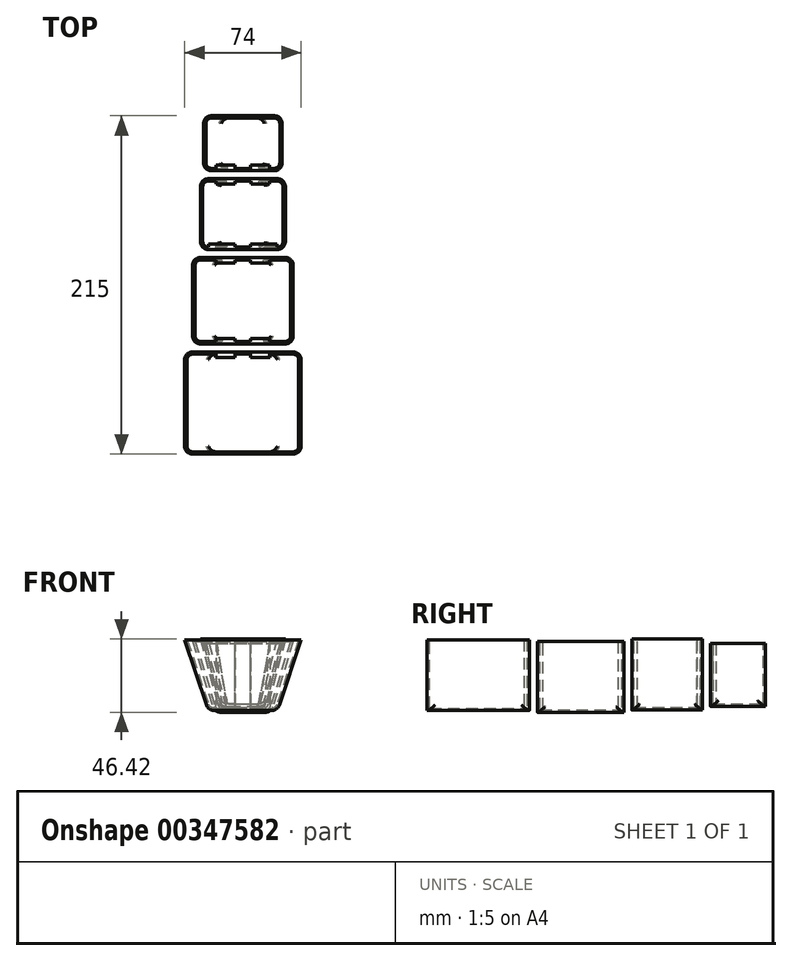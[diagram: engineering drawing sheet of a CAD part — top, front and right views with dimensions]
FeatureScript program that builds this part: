
annotation { "Feature Type Name" : "Feature", "Feature Type Description" : "" }
export const myFeature = defineFeature(function(context is Context, id is Id, definition is map)
    precondition{}
    {
        {
            var Q0;
            Q0=qCreatedBy(makeId("Front.planeOp"),FACE);
            var sketch = newSketch(context, id + "F0", { "sketchPlane" : qUnion([Q0])});
            skLineSegment(sketch, "E0", {"start": v(0, 23.9) * mm, "end": v(-37, 23.9) * mm});
            skLineSegment(sketch, "E1", {"start": v(-37, 23.9) * mm, "end": v(-22, -21.1) * mm});
            skLineSegment(sketch, "E2", {"start": v(-22, -21.1) * mm, "end": v(0, -21.1) * mm});
            skLineSegment(sketch, "E3.MirrorCS", {"start": v(0, 23.9) * mm, "end": v(37, 23.9) * mm});
            skLineSegment(sketch, "E4.MirrorCS", {"start": v(37, 23.9) * mm, "end": v(22, -21.1) * mm});
            skLineSegment(sketch, "E5.MirrorCS", {"start": v(22, -21.1) * mm, "end": v(0, -21.1) * mm});
            skSolve(sketch);
        }
        {
            var Q0;
            Q0=makeQuery(id+"F0.imprint","IMPRINT",FACE,{"disambiguationData":[TD([[makeQuery(id+"F0.imprint","IMPRINT",EDGE,{"derivedFrom":sQuery(id+"F0.wireOp",EDGE,"E0")}),1.0]])]});
            extrude(context, id + "F1", {"entities" : qUnion([Q0]), "depth" : 65 * mm});
        }
        {
            var Q0;
            Q0=makeQuery(id+"F1.opExtrude","SWEPT_EDGE",EDGE,{"disambiguationData":[OSD([sQuery(id+"F0.wireOp",EDGE,"E1"),sQuery(id+"F0.wireOp",EDGE,"E2")])]});
            var Q1;
            Q1=makeQuery(id+"F1.opExtrude","SWEPT_EDGE",EDGE,{"disambiguationData":[OSD([sQuery(id+"F0.wireOp",EDGE,"E4.MirrorCS"),sQuery(id+"F0.wireOp",EDGE,"E5.MirrorCS")])]});
            var Q2;
            Q2=makeQuery(id+"F1.opExtrude","CAP_EDGE",EDGE,{"disambiguationData":[OSD([sQuery(id+"F0.wireOp",EDGE,"E1")])],"isStart":false});
            var Q3;
            Q3=makeQuery(id+"F1.opExtrude","CAP_EDGE",EDGE,{"disambiguationData":[OSD([sQuery(id+"F0.wireOp",EDGE,"E4.MirrorCS")])],"isStart":false});
            var Q4;
            Q4=makeQuery(id+"F1.opExtrude","CAP_EDGE",EDGE,{"disambiguationData":[OSD([sQuery(id+"F0.wireOp",EDGE,"E4.MirrorCS")])],"isStart":true});
            var Q5;
            Q5=makeQuery(id+"F1.opExtrude","CAP_EDGE",EDGE,{"disambiguationData":[OSD([sQuery(id+"F0.wireOp",EDGE,"E1")])],"isStart":true});
            fillet(context, id + "F2", {"entities" : qUnion([Q0, Q1, Q2, Q3, Q4, Q5]), "radius" : 5 * mm, "tangentPropagation" : true, "allowEdgeOverflow" : false});
        }
        {
            var Q0;
            Q0=qCreatedBy(makeId("Front.planeOp"),FACE);
            cPlane(context, id + "F3", {"entities" : qUnion([Q0]), "cplaneType" : CPlaneType.OFFSET, "offset" : 60 * mm, "oppositeDirection" : true, "width" : 150 * mm, "height" : 150 * mm});
        }
        {
            var Q0;
            Q0=qCreatedBy(id+"F3.planeOp",FACE);
            var sketch = newSketch(context, id + "F4", { "sketchPlane" : qUnion([Q0])});
            skLineSegment(sketch, "E6", {"start": v(0, 22.82) * mm, "end": v(32, 22.82) * mm});
            skLineSegment(sketch, "E7", {"start": v(32, 22.82) * mm, "end": v(18, -22.18) * mm});
            skLineSegment(sketch, "E8", {"start": v(18, -22.18) * mm, "end": v(0, -22.18) * mm});
            skLineSegment(sketch, "E9.MirrorCS", {"start": v(0, 22.82) * mm, "end": v(-32, 22.82) * mm});
            skLineSegment(sketch, "E10.MirrorCS", {"start": v(-32, 22.82) * mm, "end": v(-18, -22.18) * mm});
            skLineSegment(sketch, "E11.MirrorCS", {"start": v(-18, -22.18) * mm, "end": v(0, -22.18) * mm});
            skSolve(sketch);
        }
        {
            var Q0;
            Q0=makeQuery(id+"F4.imprint","IMPRINT",FACE,{"disambiguationData":[TD([[makeQuery(id+"F4.imprint","IMPRINT",EDGE,{"derivedFrom":sQuery(id+"F4.wireOp",EDGE,"E6")}),-1.0]])]});
            extrude(context, id + "F5", {"entities" : qUnion([Q0]), "depth" : 55 * mm});
        }
        {
            var Q0;
            Q0=makeQuery(id+"F5.opExtrude","CAP_EDGE",EDGE,{"disambiguationData":[OSD([sQuery(id+"F4.wireOp",EDGE,"E7")])],"isStart":true});
            var Q1;
            Q1=makeQuery(id+"F5.opExtrude","CAP_EDGE",EDGE,{"disambiguationData":[OSD([sQuery(id+"F4.wireOp",EDGE,"E10.MirrorCS")])],"isStart":true});
            var Q2;
            Q2=makeQuery(id+"F5.opExtrude","SWEPT_EDGE",EDGE,{"disambiguationData":[OSD([sQuery(id+"F4.wireOp",EDGE,"E7"),sQuery(id+"F4.wireOp",EDGE,"E8")])]});
            var Q3;
            Q3=makeQuery(id+"F5.opExtrude","SWEPT_EDGE",EDGE,{"disambiguationData":[OSD([sQuery(id+"F4.wireOp",EDGE,"E10.MirrorCS"),sQuery(id+"F4.wireOp",EDGE,"E11.MirrorCS")])]});
            var Q4;
            Q4=makeQuery(id+"F5.opExtrude","CAP_EDGE",EDGE,{"disambiguationData":[OSD([sQuery(id+"F4.wireOp",EDGE,"E10.MirrorCS")])],"isStart":false});
            var Q5;
            Q5=makeQuery(id+"F5.opExtrude","CAP_EDGE",EDGE,{"disambiguationData":[OSD([sQuery(id+"F4.wireOp",EDGE,"E7")])],"isStart":false});
            fillet(context, id + "F6", {"entities" : qUnion([Q0, Q1, Q2, Q3, Q4, Q5]), "radius" : 5 * mm, "tangentPropagation" : true, "allowEdgeOverflow" : false});
        }
        {
            var Q0;
            Q0=qCreatedBy(id+"F3.planeOp",FACE);
            cPlane(context, id + "F7", {"entities" : qUnion([Q0]), "cplaneType" : CPlaneType.OFFSET, "offset" : 50 * mm, "oppositeDirection" : true, "width" : 150 * mm, "height" : 150 * mm});
        }
        {
            var Q0;
            Q0=qCreatedBy(id+"F7.planeOp",FACE);
            var sketch = newSketch(context, id + "F8", { "sketchPlane" : qUnion([Q0])});
            skLineSegment(sketch, "E12", {"start": v(0, 24.24) * mm, "end": v(27, 24.24) * mm});
            skLineSegment(sketch, "E13", {"start": v(27, 24.24) * mm, "end": v(15, -20.76) * mm});
            skLineSegment(sketch, "E14", {"start": v(15, -20.76) * mm, "end": v(0, -20.76) * mm});
            skLineSegment(sketch, "E15.MirrorCS", {"start": v(0, 24.24) * mm, "end": v(-27, 24.24) * mm});
            skLineSegment(sketch, "E16.MirrorCS", {"start": v(-27, 24.24) * mm, "end": v(-15, -20.76) * mm});
            skLineSegment(sketch, "E17.MirrorCS", {"start": v(-15, -20.76) * mm, "end": v(0, -20.76) * mm});
            skSolve(sketch);
        }
        {
            var Q0;
            Q0=makeQuery(id+"F8.imprint","IMPRINT",FACE,{"disambiguationData":[TD([[makeQuery(id+"F8.imprint","IMPRINT",EDGE,{"derivedFrom":sQuery(id+"F8.wireOp",EDGE,"E12")}),-1.0]])]});
            extrude(context, id + "F9", {"entities" : qUnion([Q0]), "depth" : 45 * mm});
        }
        {
            var Q0;
            Q0=makeQuery(id+"F9.opExtrude","CAP_EDGE",EDGE,{"disambiguationData":[OSD([sQuery(id+"F8.wireOp",EDGE,"E13")])],"isStart":true});
            var Q1;
            Q1=makeQuery(id+"F9.opExtrude","CAP_EDGE",EDGE,{"disambiguationData":[OSD([sQuery(id+"F8.wireOp",EDGE,"E16.MirrorCS")])],"isStart":true});
            var Q2;
            Q2=makeQuery(id+"F9.opExtrude","SWEPT_EDGE",EDGE,{"disambiguationData":[OSD([sQuery(id+"F8.wireOp",EDGE,"E13"),sQuery(id+"F8.wireOp",EDGE,"E14")])]});
            var Q3;
            Q3=makeQuery(id+"F9.opExtrude","SWEPT_EDGE",EDGE,{"disambiguationData":[OSD([sQuery(id+"F8.wireOp",EDGE,"E16.MirrorCS"),sQuery(id+"F8.wireOp",EDGE,"E17.MirrorCS")])]});
            var Q4;
            Q4=makeQuery(id+"F9.opExtrude","CAP_EDGE",EDGE,{"disambiguationData":[OSD([sQuery(id+"F8.wireOp",EDGE,"E13")])],"isStart":false});
            var Q5;
            Q5=makeQuery(id+"F9.opExtrude","CAP_EDGE",EDGE,{"disambiguationData":[OSD([sQuery(id+"F8.wireOp",EDGE,"E16.MirrorCS")])],"isStart":false});
            fillet(context, id + "F10", {"entities" : qUnion([Q0, Q1, Q2, Q3, Q4, Q5]), "radius" : 5 * mm, "tangentPropagation" : true, "allowEdgeOverflow" : false});
        }
        {
            var Q0;
            Q0=qCreatedBy(id+"F7.planeOp",FACE);
            cPlane(context, id + "F11", {"entities" : qUnion([Q0]), "cplaneType" : CPlaneType.OFFSET, "offset" : 40 * mm, "oppositeDirection" : true, "width" : 150 * mm, "height" : 150 * mm});
        }
        {
            var Q0;
            Q0=qCreatedBy(id+"F11.planeOp",FACE);
            var sketch = newSketch(context, id + "F12", { "sketchPlane" : qUnion([Q0])});
            skLineSegment(sketch, "E18", {"start": v(0, 21.5) * mm, "end": v(25, 21.5) * mm});
            skLineSegment(sketch, "E19", {"start": v(25, 21.5) * mm, "end": v(14, -18.5) * mm});
            skLineSegment(sketch, "E20", {"start": v(14, -18.5) * mm, "end": v(0, -18.5) * mm});
            skLineSegment(sketch, "E21.MirrorCS", {"start": v(0, 21.5) * mm, "end": v(-25, 21.5) * mm});
            skLineSegment(sketch, "E22.MirrorCS", {"start": v(-25, 21.5) * mm, "end": v(-14, -18.5) * mm});
            skLineSegment(sketch, "E23.MirrorCS", {"start": v(-14, -18.5) * mm, "end": v(0, -18.5) * mm});
            skSolve(sketch);
        }
        {
            var Q0;
            Q0=makeQuery(id+"F12.imprint","IMPRINT",FACE,{"disambiguationData":[TD([[makeQuery(id+"F12.imprint","IMPRINT",EDGE,{"derivedFrom":sQuery(id+"F12.wireOp",EDGE,"E18")}),-1.0]])]});
            extrude(context, id + "F13", {"entities" : qUnion([Q0]), "depth" : 35 * mm});
        }
        {
            var Q0;
            Q0=makeQuery(id+"F13.opExtrude","CAP_EDGE",EDGE,{"disambiguationData":[OSD([sQuery(id+"F12.wireOp",EDGE,"E19")])],"isStart":true});
            var Q1;
            Q1=makeQuery(id+"F13.opExtrude","CAP_EDGE",EDGE,{"disambiguationData":[OSD([sQuery(id+"F12.wireOp",EDGE,"E22.MirrorCS")])],"isStart":true});
            var Q2;
            Q2=makeQuery(id+"F13.opExtrude","SWEPT_EDGE",EDGE,{"disambiguationData":[OSD([sQuery(id+"F12.wireOp",EDGE,"E19"),sQuery(id+"F12.wireOp",EDGE,"E20")])]});
            var Q3;
            Q3=makeQuery(id+"F13.opExtrude","SWEPT_EDGE",EDGE,{"disambiguationData":[OSD([sQuery(id+"F12.wireOp",EDGE,"E22.MirrorCS"),sQuery(id+"F12.wireOp",EDGE,"E23.MirrorCS")])]});
            var Q4;
            Q4=makeQuery(id+"F13.opExtrude","CAP_EDGE",EDGE,{"disambiguationData":[OSD([sQuery(id+"F12.wireOp",EDGE,"E19")])],"isStart":false});
            var Q5;
            Q5=makeQuery(id+"F13.opExtrude","CAP_EDGE",EDGE,{"disambiguationData":[OSD([sQuery(id+"F12.wireOp",EDGE,"E22.MirrorCS")])],"isStart":false});
            fillet(context, id + "F14", {"entities" : qUnion([Q0, Q1, Q2, Q3, Q4, Q5]), "radius" : 5 * mm, "tangentPropagation" : true, "allowEdgeOverflow" : false});
        }
        {
            var Q0;
            Q0=makeQuery(id+"F5.opExtrude","SWEPT_FACE",FACE,{"disambiguationData":[OSD([sQuery(id+"F4.wireOp",EDGE,"E6"),sQuery(id+"F4.wireOp",EDGE,"E9.MirrorCS")])]});
            shell(context, id + "F15", {"entities" : qUnion([Q0]), "thickness" : 1.6 * mm});
        }
        {
            var Q0;
            Q0=makeQuery(id+"F13.opExtrude","SWEPT_FACE",FACE,{"disambiguationData":[OSD([sQuery(id+"F12.wireOp",EDGE,"E18"),sQuery(id+"F12.wireOp",EDGE,"E21.MirrorCS")])]});
            shell(context, id + "F16", {"entities" : qUnion([Q0]), "thickness" : 1.5 * mm});
        }
        {
            var Q0;
            Q0=makeQuery(id+"F1.opExtrude","SWEPT_FACE",FACE,{"disambiguationData":[OSD([sQuery(id+"F0.wireOp",EDGE,"E0"),sQuery(id+"F0.wireOp",EDGE,"E3.MirrorCS")])]});
            shell(context, id + "F17", {"entities" : qUnion([Q0]), "thickness" : 1.5 * mm});
        }
        {
            var Q0;
            Q0=makeQuery(id+"F9.opExtrude","SWEPT_FACE",FACE,{"disambiguationData":[OSD([sQuery(id+"F8.wireOp",EDGE,"E12"),sQuery(id+"F8.wireOp",EDGE,"E15.MirrorCS")])]});
            shell(context, id + "F18", {"entities" : qUnion([Q0]), "thickness" : 1.5 * mm});
        }
        {
            var Q0;
            {var subQ0=sQuery(id+"F8.wireOp",EDGE,"E17.MirrorCS");var subQ1=sQuery(id+"F8.wireOp",EDGE,"E16.MirrorCS");var subQ2=sQuery(id+"F8.wireOp",EDGE,"E15.MirrorCS");var subQ3=sQuery(id+"F8.wireOp",EDGE,"E14");var subQ4=sQuery(id+"F8.wireOp",EDGE,"E13");var subQ5=sQuery(id+"F8.wireOp",EDGE,"E12");Q0=makeQuery(id+"F18.opShell","OFFSET_FACE",FACE,{"disambiguationData":[OSD([subQ5,subQ4,subQ3,subQ2,subQ1,subQ0]),TDD([makeQuery(id+"F9.opExtrude","CAP_FACE",FACE,{"disambiguationData":[OSD([subQ5,subQ4,subQ3,subQ2,subQ1,subQ0])],"isStart":true})])]});}
            var sketch = newSketch(context, id + "F19", { "sketchPlane" : qUnion([Q0])});
            skLineSegment(sketch, "E24", {"start": v(-5, -19.26) * mm, "end": v(-5, 24.24) * mm});
            skLineSegment(sketch, "E25", {"start": v(-5, 24.24) * mm, "end": v(-17, 24.24) * mm});
            skLineSegment(sketch, "E26", {"start": v(-17, 24.24) * mm, "end": v(-10.23, -19.26) * mm});
            skLineSegment(sketch, "E27", {"start": v(-10.23, -19.26) * mm, "end": v(-5, -19.26) * mm});
            skLineSegment(sketch, "E28", {"start": v(0.03, -19.26) * mm, "end": v(0.03, 24.24) * mm, "construction": true});
            skLineSegment(sketch, "E29.MirrorCS", {"start": v(5.05, -19.26) * mm, "end": v(5.05, 24.24) * mm});
            skLineSegment(sketch, "E30.MirrorCS", {"start": v(5.05, 24.24) * mm, "end": v(17.05, 24.24) * mm});
            skLineSegment(sketch, "E31.MirrorCS", {"start": v(17.05, 24.24) * mm, "end": v(10.28, -19.26) * mm});
            skLineSegment(sketch, "E32.MirrorCS", {"start": v(10.28, -19.26) * mm, "end": v(5.05, -19.26) * mm});
            skSolve(sketch);
        }
        {
            var Q0;
            Q0=makeQuery(id+"F19.imprint","IMPRINT",FACE,{"disambiguationData":[TD([[makeQuery(id+"F19.imprint","IMPRINT",EDGE,{"derivedFrom":sQuery(id+"F19.wireOp",EDGE,"0ba9f9f1-b0b3-4cc9-8b6a-4698d6627ffc0.MirrorCS")}),-1.0]])]});
            var Q1;
            Q1=makeQuery(id+"F19.imprint","IMPRINT",FACE,{"disambiguationData":[TD([[makeQuery(id+"F19.imprint","IMPRINT",EDGE,{"derivedFrom":sQuery(id+"F19.wireOp",EDGE,"E24")}),1.0]])]});
            var Q2;
            {var subQ12=sQuery(id+"F19.wireOp",EDGE,"E29.MirrorCS");Q2=makeQuery(id+"F19.imprint","IMPRINT",FACE,{"disambiguationData":[TD([[makeQuery(id+"F19.imprint","IMPRINT",EDGE,{"derivedFrom":subQ12}),-1.0]])]});}
            extrude(context, id + "F20", {"entities" : qUnion([Q0, Q1, Q2]), "operationType" : NewBodyOperationType.ADD, "depth" : 2 * mm});
        }
        {
            var Q0;
            {var subQ0=sQuery(id+"F8.wireOp",EDGE,"E17.MirrorCS");var subQ1=sQuery(id+"F8.wireOp",EDGE,"E16.MirrorCS");var subQ2=sQuery(id+"F8.wireOp",EDGE,"E15.MirrorCS");var subQ3=sQuery(id+"F8.wireOp",EDGE,"E14");var subQ4=sQuery(id+"F8.wireOp",EDGE,"E13");var subQ5=sQuery(id+"F8.wireOp",EDGE,"E12");Q0=makeQuery(id+"F18.opShell","OFFSET_FACE",FACE,{"disambiguationData":[OSD([subQ5,subQ4,subQ3,subQ2,subQ1,subQ0]),TDD([makeQuery(id+"F9.opExtrude","CAP_FACE",FACE,{"disambiguationData":[OSD([subQ5,subQ4,subQ3,subQ2,subQ1,subQ0])],"isStart":false})])]});}
            var sketch = newSketch(context, id + "F21", { "sketchPlane" : qUnion([Q0])});
            skLineSegment(sketch, "E33", {"start": v(0, -19.26) * mm, "end": v(0, 24.24) * mm, "construction": true});
            skPoint(sketch, "E34.0", {"position": v(-10.23, -19.26) * mm});
            skPoint(sketch, "E35.0", {"position": v(10.23, -19.26) * mm});
            skPoint(sketch, "E36.0", {"position": v(21.83, 24.24) * mm});
            skPoint(sketch, "E37.0", {"position": v(-21.83, 24.24) * mm});
            skLineSegment(sketch, "E38.0", {"start": v(10.23, -19.26) * mm, "end": v(-10.23, -19.26) * mm});
            skLineSegment(sketch, "E39", {"start": v(-5, -19.26) * mm, "end": v(-5, 24.24) * mm});
            skLineSegment(sketch, "E40", {"start": v(-5, -19.26) * mm, "end": v(-10.23, -19.26) * mm});
            skLineSegment(sketch, "E41", {"start": v(-21.83, 24.24) * mm, "end": v(-5, 24.24) * mm});
            skLineSegment(sketch, "E42.MirrorCS", {"start": v(5, -19.26) * mm, "end": v(5, 24.24) * mm});
            skLineSegment(sketch, "E43.MirrorCS", {"start": v(5, -19.26) * mm, "end": v(10.23, -19.26) * mm});
            skLineSegment(sketch, "E44.MirrorCS", {"start": v(21.83, 24.24) * mm, "end": v(5, 24.24) * mm});
            skLineSegment(sketch, "E45", {"start": v(-10.23, -19.26) * mm, "end": v(-21.83, 24.24) * mm});
            skLineSegment(sketch, "E46.MirrorCS", {"start": v(10.23, -19.26) * mm, "end": v(21.83, 24.24) * mm});
            skSolve(sketch);
        }
        {
            var Q0;
            Q0=makeQuery(id+"F21.imprint","IMPRINT",FACE,{"disambiguationData":[TD([[makeQuery(id+"F21.imprint","IMPRINT",EDGE,{"derivedFrom":sQuery(id+"F21.wireOp",EDGE,"E39")}),1.0]])]});
            var Q1;
            Q1=makeQuery(id+"F21.imprint","IMPRINT",FACE,{"disambiguationData":[TD([[makeQuery(id+"F21.imprint","IMPRINT",EDGE,{"derivedFrom":sQuery(id+"F21.wireOp",EDGE,"E42.MirrorCS")}),-1.0]])]});
            extrude(context, id + "F22", {"entities" : qUnion([Q0, Q1]), "operationType" : NewBodyOperationType.ADD, "depth" : 2 * mm});
        }
        {
            var Q0;
            {var subQ0=sQuery(id+"F12.wireOp",EDGE,"E23.MirrorCS");var subQ1=sQuery(id+"F12.wireOp",EDGE,"E22.MirrorCS");var subQ2=sQuery(id+"F12.wireOp",EDGE,"E21.MirrorCS");var subQ3=sQuery(id+"F12.wireOp",EDGE,"E20");var subQ4=sQuery(id+"F12.wireOp",EDGE,"E19");var subQ5=sQuery(id+"F12.wireOp",EDGE,"E18");Q0=makeQuery(id+"F16.opShell","OFFSET_FACE",FACE,{"disambiguationData":[OSD([subQ5,subQ4,subQ3,subQ2,subQ1,subQ0]),TDD([makeQuery(id+"F13.opExtrude","CAP_FACE",FACE,{"disambiguationData":[OSD([subQ5,subQ4,subQ3,subQ2,subQ1,subQ0])],"isStart":false})])]});}
            var sketch = newSketch(context, id + "F23", { "sketchPlane" : qUnion([Q0])});
            skLineSegment(sketch, "E47", {"start": v(0, -17) * mm, "end": v(0, 21.5) * mm, "construction": true});
            skLineSegment(sketch, "E48", {"start": v(-5, -17) * mm, "end": v(-5, 21.5) * mm});
            skLineSegment(sketch, "E49", {"start": v(-5, -17) * mm, "end": v(-10, -17) * mm});
            skLineSegment(sketch, "E50", {"start": v(-17, 21.5) * mm, "end": v(-5, 21.5) * mm});
            skLineSegment(sketch, "E51.MirrorCS", {"start": v(5, -17) * mm, "end": v(5, 21.5) * mm});
            skLineSegment(sketch, "E52.MirrorCS", {"start": v(5, -17) * mm, "end": v(10, -17) * mm});
            skLineSegment(sketch, "E53.MirrorCS", {"start": v(17, 21.5) * mm, "end": v(5, 21.5) * mm});
            skLineSegment(sketch, "E54", {"start": v(-17, 21.5) * mm, "end": v(-10, -17) * mm});
            skLineSegment(sketch, "E55", {"start": v(17, 21.5) * mm, "end": v(10, -17) * mm});
            skSolve(sketch);
        }
        {
            var Q0;
            Q0 = qSketchRegion(id + "F23", true);
            var Q1;
            Q1=makeQuery(id+"F23.imprint","IMPRINT",FACE,{"disambiguationData":[TD([[makeQuery(id+"F23.imprint","IMPRINT",EDGE,{"derivedFrom":sQuery(id+"F23.wireOp",EDGE,"E51.MirrorCS")}),-1.0]])]});
            extrude(context, id + "F24", {"entities" : qUnion([Q0, Q1]), "operationType" : NewBodyOperationType.ADD, "depth" : 2 * mm});
        }
        {
            var Q0;
            {var subQ0=sQuery(id+"F4.wireOp",EDGE,"E11.MirrorCS");var subQ1=sQuery(id+"F4.wireOp",EDGE,"E10.MirrorCS");var subQ2=sQuery(id+"F4.wireOp",EDGE,"E9.MirrorCS");var subQ3=sQuery(id+"F4.wireOp",EDGE,"E8");var subQ4=sQuery(id+"F4.wireOp",EDGE,"E7");var subQ5=sQuery(id+"F4.wireOp",EDGE,"E6");Q0=makeQuery(id+"F15.opShell","OFFSET_FACE",FACE,{"disambiguationData":[OSD([subQ5,subQ4,subQ3,subQ2,subQ1,subQ0]),TDD([makeQuery(id+"F5.opExtrude","CAP_FACE",FACE,{"disambiguationData":[OSD([subQ5,subQ4,subQ3,subQ2,subQ1,subQ0])],"isStart":true})])]});}
            var sketch = newSketch(context, id + "F25", { "sketchPlane" : qUnion([Q0])});
            skLineSegment(sketch, "E56", {"start": v(0, 22.82) * mm, "end": v(0, -20.58) * mm, "construction": true});
            skLineSegment(sketch, "E57", {"start": v(-5, 22.82) * mm, "end": v(-5, -20.58) * mm});
            skLineSegment(sketch, "E58", {"start": v(-5, 22.82) * mm, "end": v(-17, 22.82) * mm});
            skLineSegment(sketch, "E59", {"start": v(-17, 22.82) * mm, "end": v(-13.26, -20.58) * mm});
            skLineSegment(sketch, "E60", {"start": v(-13.26, -20.58) * mm, "end": v(-5, -20.58) * mm});
            skLineSegment(sketch, "E61.MirrorCS", {"start": v(5, 22.82) * mm, "end": v(5, -20.58) * mm});
            skLineSegment(sketch, "E62.MirrorCS", {"start": v(5, 22.82) * mm, "end": v(17, 22.82) * mm});
            skLineSegment(sketch, "E63.MirrorCS", {"start": v(17, 22.82) * mm, "end": v(13.26, -20.58) * mm});
            skLineSegment(sketch, "E64.MirrorCS", {"start": v(13.26, -20.58) * mm, "end": v(5, -20.58) * mm});
            skSolve(sketch);
        }
        {
            var Q0;
            Q0 = qSketchRegion(id + "F25", true);
            extrude(context, id + "F26", {"entities" : qUnion([Q0]), "operationType" : NewBodyOperationType.ADD, "depth" : 2 * mm});
        }
        {
            var Q0;
            {var subQ0=sQuery(id+"F4.wireOp",EDGE,"E11.MirrorCS");var subQ1=sQuery(id+"F4.wireOp",EDGE,"E10.MirrorCS");var subQ2=sQuery(id+"F4.wireOp",EDGE,"E9.MirrorCS");var subQ3=sQuery(id+"F4.wireOp",EDGE,"E8");var subQ4=sQuery(id+"F4.wireOp",EDGE,"E7");var subQ5=sQuery(id+"F4.wireOp",EDGE,"E6");Q0=makeQuery(id+"F15.opShell","OFFSET_FACE",FACE,{"disambiguationData":[OSD([subQ5,subQ4,subQ3,subQ2,subQ1,subQ0]),TDD([makeQuery(id+"F5.opExtrude","CAP_FACE",FACE,{"disambiguationData":[OSD([subQ5,subQ4,subQ3,subQ2,subQ1,subQ0])],"isStart":false})])]});}
            var sketch = newSketch(context, id + "F27", { "sketchPlane" : qUnion([Q0])});
            skLineSegment(sketch, "E65", {"start": v(0, -20.58) * mm, "end": v(0, 22.82) * mm, "construction": true});
            skLineSegment(sketch, "E66", {"start": v(-5, -20.58) * mm, "end": v(-5, 22.82) * mm});
            skLineSegment(sketch, "E67", {"start": v(-5, -20.58) * mm, "end": v(-13.26, -20.58) * mm});
            skLineSegment(sketch, "E68", {"start": v(-13.26, -20.58) * mm, "end": v(-17, 22.82) * mm});
            skLineSegment(sketch, "E69", {"start": v(-17, 22.82) * mm, "end": v(-5, 22.82) * mm});
            skLineSegment(sketch, "E70.MirrorCS", {"start": v(5, -20.58) * mm, "end": v(5, 22.82) * mm});
            skLineSegment(sketch, "E71.MirrorCS", {"start": v(5, -20.58) * mm, "end": v(13.26, -20.58) * mm});
            skLineSegment(sketch, "E72.MirrorCS", {"start": v(13.26, -20.58) * mm, "end": v(17, 22.82) * mm});
            skLineSegment(sketch, "E73.MirrorCS", {"start": v(17, 22.82) * mm, "end": v(5, 22.82) * mm});
            skSolve(sketch);
        }
        {
            var Q0;
            Q0=makeQuery(id+"F27.imprint","IMPRINT",FACE,{"disambiguationData":[TD([[makeQuery(id+"F27.imprint","IMPRINT",EDGE,{"derivedFrom":sQuery(id+"F27.wireOp",EDGE,"E70.MirrorCS")}),-1.0]])]});
            var Q1;
            Q1=makeQuery(id+"F27.imprint","IMPRINT",FACE,{"disambiguationData":[TD([[makeQuery(id+"F27.imprint","IMPRINT",EDGE,{"derivedFrom":sQuery(id+"F27.wireOp",EDGE,"E66")}),1.0]])]});
            extrude(context, id + "F28", {"entities" : qUnion([Q0, Q1]), "operationType" : NewBodyOperationType.ADD, "depth" : 2 * mm});
        }
        {
            var Q0;
            {var subQ0=sQuery(id+"F0.wireOp",EDGE,"E5.MirrorCS");var subQ1=sQuery(id+"F0.wireOp",EDGE,"E4.MirrorCS");var subQ2=sQuery(id+"F0.wireOp",EDGE,"E3.MirrorCS");var subQ3=sQuery(id+"F0.wireOp",EDGE,"E2");var subQ4=sQuery(id+"F0.wireOp",EDGE,"E1");var subQ5=sQuery(id+"F0.wireOp",EDGE,"E0");Q0=makeQuery(id+"F17.opShell","OFFSET_FACE",FACE,{"disambiguationData":[OSD([subQ5,subQ4,subQ3,subQ2,subQ1,subQ0]),TDD([makeQuery(id+"F1.opExtrude","CAP_FACE",FACE,{"disambiguationData":[OSD([subQ5,subQ4,subQ3,subQ2,subQ1,subQ0])],"isStart":true})])]});}
            var sketch = newSketch(context, id + "F29", { "sketchPlane" : qUnion([Q0])});
            skLineSegment(sketch, "E74", {"start": v(0, -19.6) * mm, "end": v(0, 23.9) * mm, "construction": true});
            skLineSegment(sketch, "E75", {"start": v(-5, 23.9) * mm, "end": v(-5, -19.6) * mm});
            skLineSegment(sketch, "E76", {"start": v(-5, 23.9) * mm, "end": v(-31.73, 23.9) * mm});
            skLineSegment(sketch, "E77", {"start": v(-17, 23.9) * mm, "end": v(-17.23, -19.6) * mm});
            skLineSegment(sketch, "E78", {"start": v(-17.23, -19.6) * mm, "end": v(-5, -19.6) * mm});
            skLineSegment(sketch, "E79.MirrorCS", {"start": v(5, 23.9) * mm, "end": v(5, -19.6) * mm});
            skLineSegment(sketch, "E80.MirrorCS", {"start": v(5, 23.9) * mm, "end": v(31.73, 23.9) * mm});
            skLineSegment(sketch, "E81.MirrorCS", {"start": v(17, 23.9) * mm, "end": v(17.23, -19.6) * mm});
            skLineSegment(sketch, "E82.MirrorCS", {"start": v(17.23, -19.6) * mm, "end": v(5, -19.6) * mm});
            skSolve(sketch);
        }
        {
            var Q0;
            Q0 = qSketchRegion(id + "F29", true);
            extrude(context, id + "F30", {"entities" : qUnion([Q0]), "operationType" : NewBodyOperationType.ADD, "depth" : 2 * mm});
        }
    });
